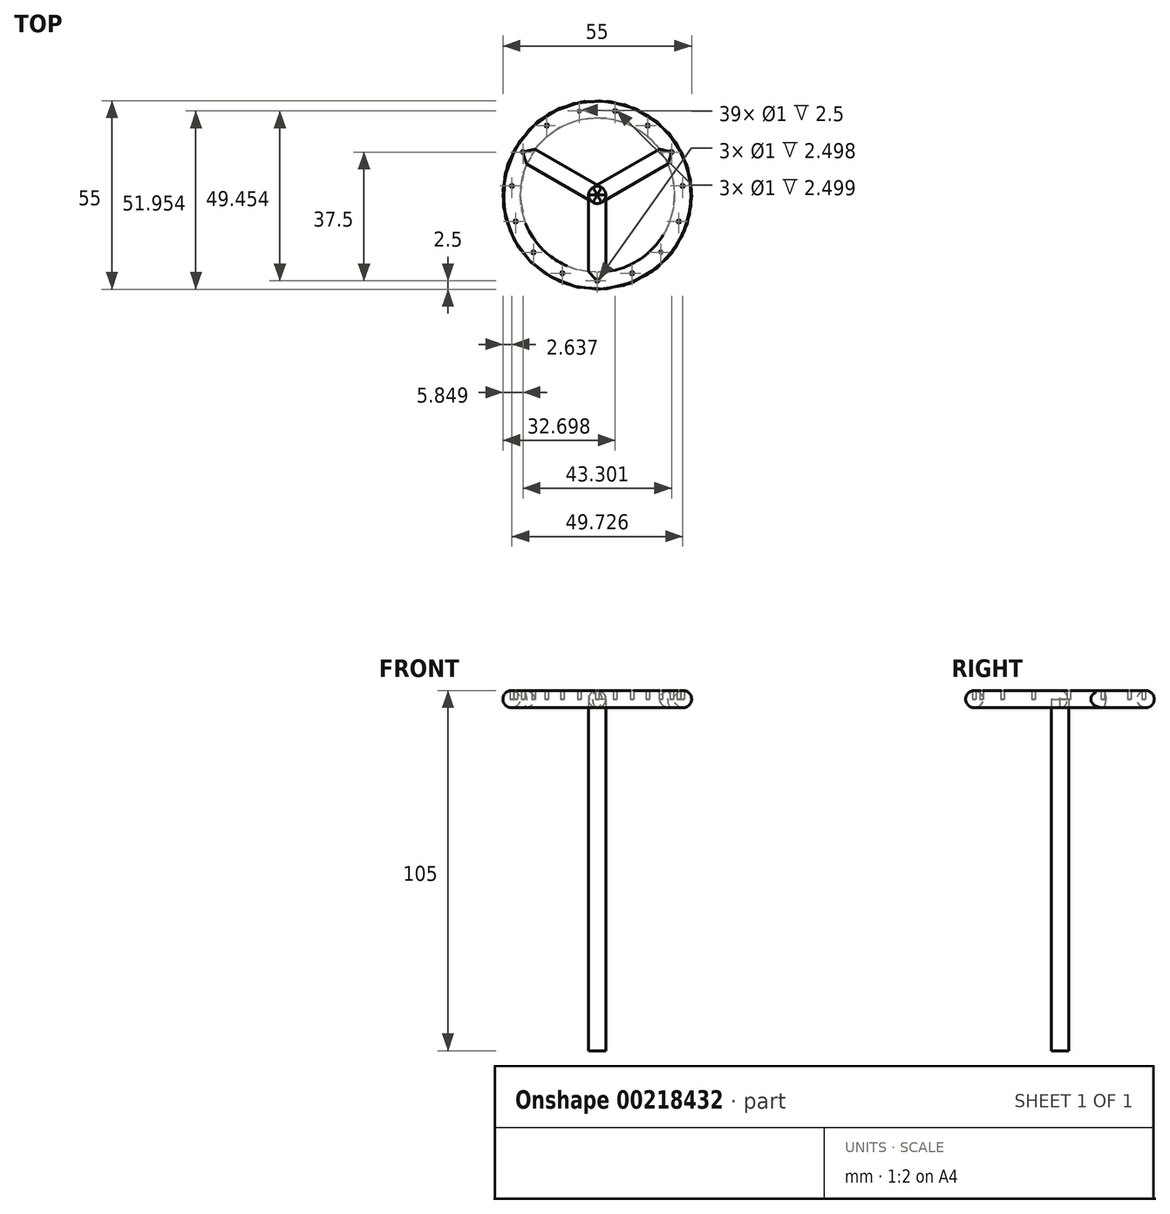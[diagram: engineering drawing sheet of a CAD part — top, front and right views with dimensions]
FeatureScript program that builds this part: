
annotation { "Feature Type Name" : "Feature", "Feature Type Description" : "" }
export const myFeature = defineFeature(function(context is Context, id is Id, definition is map)
    precondition{}
    {
        {
            var Q0;
            Q0=qCreatedBy(makeId("Top.planeOp"),FACE);
            var sketch = newSketch(context, id + "F0", { "sketchPlane" : qUnion([Q0])});
            skCircle(sketch, "E0", {"center": v(0, 0) * mm, "radius": 25 * mm});
            skLineSegment(sketch, "E1", {"start": v(0, 0) * mm, "end": v(-21.65, 12.5) * mm});
            skLineSegment(sketch, "E2", {"start": v(0, 0) * mm, "end": v(21.65, 12.5) * mm});
            skLineSegment(sketch, "E3", {"start": v(0, 0) * mm, "end": v(0, -25) * mm});
            skSolve(sketch);
        }
        {
            var Q0;
            Q0=qCreatedBy(makeId("Front.planeOp"),FACE);
            var sketch = newSketch(context, id + "F1", { "sketchPlane" : qUnion([Q0])});
            skLineSegment(sketch, "E4", {"start": v(0, 0) * mm, "end": v(0, -102.5) * mm});
            skSolve(sketch);
        }
        {
            var Q0;
            Q0=qCreatedBy(makeId("Front.planeOp"),FACE);
            var sketch = newSketch(context, id + "F2", { "sketchPlane" : qUnion([Q0])});
            skCircle(sketch, "E5", {"center": v(-25, 0) * mm, "radius": 2.5 * mm});
            skSolve(sketch);
        }
        {
            var Q0;
            Q0=makeQuery(id+"F2.imprint","IMPRINT",FACE,{"disambiguationData":[TD([[makeQuery(id+"F2.imprint","IMPRINT",EDGE,{"derivedFrom":sQuery(id+"F2.wireOp",EDGE,"E5")}),1.0]])]});
            var Q1;
            Q1=sQuery(id+"F0.wireOp",EDGE,"E0");
            sweep(context, id + "F3", {"profiles" : qUnion([Q0]), "path" : qUnion([Q1])});
        }
        {
            var Q0;
            Q0=qCreatedBy(makeId("Front.planeOp"),FACE);
            var sketch = newSketch(context, id + "F4", { "sketchPlane" : qUnion([Q0])});
            skCircle(sketch, "E6", {"center": v(0, 0) * mm, "radius": 2.5 * mm});
            skSolve(sketch);
        }
        {
            var Q0;
            Q0=makeQuery(id+"F4.imprint","IMPRINT",FACE,{"disambiguationData":[TD([[makeQuery(id+"F4.imprint","IMPRINT",EDGE,{"derivedFrom":sQuery(id+"F4.wireOp",EDGE,"E6")}),1.0]])]});
            var Q1;
            Q1=sQuery(id+"F0.wireOp",EDGE,"E3");
            sweep(context, id + "F5", {"operationType" : NewBodyOperationType.ADD, "profiles" : qUnion([Q0]), "path" : qUnion([Q1])});
        }
        {
            var Q0;
            Q0=makeQuery(id+"F3.opSweep","SWEPT_BODY",BODY,{"disambiguationData":[OSD([sQuery(id+"F0.wireOp",EDGE,"E0"),sQuery(id+"F2.wireOp",EDGE,"E5")])]});
            var Q1;
            Q1=sQuery(id+"F1.wireOp",EDGE,"E4");
            circularPattern(context, id + "F6", {"entities" : qUnion([Q0]), "axis" : qUnion([Q1]), "angle" : 360 * degree, "instanceCount" : 3, "equalSpace" : true});
        }
        {
            var Q0;
            Q0=qCreatedBy(makeId("Top.planeOp"),FACE);
            var sketch = newSketch(context, id + "F7", { "sketchPlane" : qUnion([Q0])});
            skCircle(sketch, "E7", {"center": v(0, 0) * mm, "radius": 2.5 * mm});
            skSolve(sketch);
        }
        {
            var Q0;
            Q0 = qSketchRegion(id + "F7", true);
            var Q1;
            Q1=sQuery(id+"F1.wireOp",EDGE,"E4");
            sweep(context, id + "F8", {"profiles" : qUnion([Q0]), "path" : qUnion([Q1])});
        }
        {
            var Q0;
            Q0=qCreatedBy(makeId("Top.planeOp"),FACE);
            var sketch = newSketch(context, id + "F9", { "sketchPlane" : qUnion([Q0])});
            skCircle(sketch, "E8", {"center": v(0, -25) * mm, "radius": 0.5 * mm});
            skSolve(sketch);
        }
        {
            var Q0;
            Q0 = qSketchRegion(id + "F9", true);
            extrude(context, id + "F10", {"entities" : qUnion([Q0]), "depth" : 2.5 * mm});
        }
        {
            var Q0;
            Q0=makeQuery(id+"F10.opExtrude","SWEPT_BODY",BODY,{"disambiguationData":[OSD([sQuery(id+"F9.wireOp",EDGE,"E8")])]});
            var Q1;
            Q1=sQuery(id+"F1.wireOp",EDGE,"E4");
            circularPattern(context, id + "F11", {"entities" : qUnion([Q0]), "axis" : qUnion([Q1]), "angle" : 360 * degree, "instanceCount" : 15, "equalSpace" : true});
        }
        {
            var Q0;
            Q0=makeQuery(id+"F11.opPattern","COPY",BODY,{"derivedFrom":makeQuery(id+"F10.opExtrude","SWEPT_BODY",BODY,{"disambiguationData":[OSD([sQuery(id+"F9.wireOp",EDGE,"E8")])]}),"instanceName":"1"});
            var Q1;
            Q1=makeQuery(id+"F11.opPattern","COPY",BODY,{"derivedFrom":makeQuery(id+"F10.opExtrude","SWEPT_BODY",BODY,{"disambiguationData":[OSD([sQuery(id+"F9.wireOp",EDGE,"E8")])]}),"instanceName":"23"});
            var Q2;
            Q2=makeQuery(id+"F11.opPattern","COPY",BODY,{"derivedFrom":makeQuery(id+"F10.opExtrude","SWEPT_BODY",BODY,{"disambiguationData":[OSD([sQuery(id+"F9.wireOp",EDGE,"E8")])]}),"instanceName":"22"});
            var Q3;
            Q3=makeQuery(id+"F11.opPattern","COPY",BODY,{"derivedFrom":makeQuery(id+"F10.opExtrude","SWEPT_BODY",BODY,{"disambiguationData":[OSD([sQuery(id+"F9.wireOp",EDGE,"E8")])]}),"instanceName":"21"});
            var Q4;
            Q4=makeQuery(id+"F11.opPattern","COPY",BODY,{"derivedFrom":makeQuery(id+"F10.opExtrude","SWEPT_BODY",BODY,{"disambiguationData":[OSD([sQuery(id+"F9.wireOp",EDGE,"E8")])]}),"instanceName":"20"});
            var Q5;
            Q5=makeQuery(id+"F11.opPattern","COPY",BODY,{"derivedFrom":makeQuery(id+"F10.opExtrude","SWEPT_BODY",BODY,{"disambiguationData":[OSD([sQuery(id+"F9.wireOp",EDGE,"E8")])]}),"instanceName":"19"});
            var Q6;
            Q6=makeQuery(id+"F11.opPattern","COPY",BODY,{"derivedFrom":makeQuery(id+"F10.opExtrude","SWEPT_BODY",BODY,{"disambiguationData":[OSD([sQuery(id+"F9.wireOp",EDGE,"E8")])]}),"instanceName":"18"});
            var Q7;
            Q7=makeQuery(id+"F11.opPattern","COPY",BODY,{"derivedFrom":makeQuery(id+"F10.opExtrude","SWEPT_BODY",BODY,{"disambiguationData":[OSD([sQuery(id+"F9.wireOp",EDGE,"E8")])]}),"instanceName":"17"});
            var Q8;
            Q8=makeQuery(id+"F11.opPattern","COPY",BODY,{"derivedFrom":makeQuery(id+"F10.opExtrude","SWEPT_BODY",BODY,{"disambiguationData":[OSD([sQuery(id+"F9.wireOp",EDGE,"E8")])]}),"instanceName":"16"});
            var Q9;
            Q9=makeQuery(id+"F11.opPattern","COPY",BODY,{"derivedFrom":makeQuery(id+"F10.opExtrude","SWEPT_BODY",BODY,{"disambiguationData":[OSD([sQuery(id+"F9.wireOp",EDGE,"E8")])]}),"instanceName":"15"});
            var Q10;
            Q10=makeQuery(id+"F11.opPattern","COPY",BODY,{"derivedFrom":makeQuery(id+"F10.opExtrude","SWEPT_BODY",BODY,{"disambiguationData":[OSD([sQuery(id+"F9.wireOp",EDGE,"E8")])]}),"instanceName":"14"});
            var Q11;
            Q11=makeQuery(id+"F11.opPattern","COPY",BODY,{"derivedFrom":makeQuery(id+"F10.opExtrude","SWEPT_BODY",BODY,{"disambiguationData":[OSD([sQuery(id+"F9.wireOp",EDGE,"E8")])]}),"instanceName":"13"});
            var Q12;
            Q12=makeQuery(id+"F11.opPattern","COPY",BODY,{"derivedFrom":makeQuery(id+"F10.opExtrude","SWEPT_BODY",BODY,{"disambiguationData":[OSD([sQuery(id+"F9.wireOp",EDGE,"E8")])]}),"instanceName":"12"});
            var Q13;
            Q13=makeQuery(id+"F11.opPattern","COPY",BODY,{"derivedFrom":makeQuery(id+"F10.opExtrude","SWEPT_BODY",BODY,{"disambiguationData":[OSD([sQuery(id+"F9.wireOp",EDGE,"E8")])]}),"instanceName":"11"});
            var Q14;
            Q14=makeQuery(id+"F11.opPattern","COPY",BODY,{"derivedFrom":makeQuery(id+"F10.opExtrude","SWEPT_BODY",BODY,{"disambiguationData":[OSD([sQuery(id+"F9.wireOp",EDGE,"E8")])]}),"instanceName":"10"});
            var Q15;
            Q15=makeQuery(id+"F11.opPattern","COPY",BODY,{"derivedFrom":makeQuery(id+"F10.opExtrude","SWEPT_BODY",BODY,{"disambiguationData":[OSD([sQuery(id+"F9.wireOp",EDGE,"E8")])]}),"instanceName":"9"});
            var Q16;
            Q16=makeQuery(id+"F11.opPattern","COPY",BODY,{"derivedFrom":makeQuery(id+"F10.opExtrude","SWEPT_BODY",BODY,{"disambiguationData":[OSD([sQuery(id+"F9.wireOp",EDGE,"E8")])]}),"instanceName":"8"});
            var Q17;
            Q17=makeQuery(id+"F11.opPattern","COPY",BODY,{"derivedFrom":makeQuery(id+"F10.opExtrude","SWEPT_BODY",BODY,{"disambiguationData":[OSD([sQuery(id+"F9.wireOp",EDGE,"E8")])]}),"instanceName":"7"});
            var Q18;
            Q18=makeQuery(id+"F11.opPattern","COPY",BODY,{"derivedFrom":makeQuery(id+"F10.opExtrude","SWEPT_BODY",BODY,{"disambiguationData":[OSD([sQuery(id+"F9.wireOp",EDGE,"E8")])]}),"instanceName":"6"});
            var Q19;
            Q19=makeQuery(id+"F11.opPattern","COPY",BODY,{"derivedFrom":makeQuery(id+"F10.opExtrude","SWEPT_BODY",BODY,{"disambiguationData":[OSD([sQuery(id+"F9.wireOp",EDGE,"E8")])]}),"instanceName":"5"});
            var Q20;
            Q20=makeQuery(id+"F11.opPattern","COPY",BODY,{"derivedFrom":makeQuery(id+"F10.opExtrude","SWEPT_BODY",BODY,{"disambiguationData":[OSD([sQuery(id+"F9.wireOp",EDGE,"E8")])]}),"instanceName":"4"});
            var Q21;
            Q21=makeQuery(id+"F11.opPattern","COPY",BODY,{"derivedFrom":makeQuery(id+"F10.opExtrude","SWEPT_BODY",BODY,{"disambiguationData":[OSD([sQuery(id+"F9.wireOp",EDGE,"E8")])]}),"instanceName":"3"});
            var Q22;
            Q22=makeQuery(id+"F11.opPattern","COPY",BODY,{"derivedFrom":makeQuery(id+"F10.opExtrude","SWEPT_BODY",BODY,{"disambiguationData":[OSD([sQuery(id+"F9.wireOp",EDGE,"E8")])]}),"instanceName":"2"});
            var Q23;
            Q23=makeQuery(id+"FsdLYlgyIIPtPH4_3.opPattern","COPY",BODY,{"derivedFrom":makeQuery(id+"F10.opExtrude","SWEPT_BODY",BODY,{"disambiguationData":[OSD([sQuery(id+"F9.wireOp",EDGE,"E8")])]}),"instanceName":"1"});
            var Q24;
            Q24=makeQuery(id+"FsdLYlgyIIPtPH4_3.opPattern","COPY",BODY,{"derivedFrom":makeQuery(id+"F10.opExtrude","SWEPT_BODY",BODY,{"disambiguationData":[OSD([sQuery(id+"F9.wireOp",EDGE,"E8")])]}),"instanceName":"2"});
            var Q25;
            Q25=makeQuery(id+"F10.opExtrude","SWEPT_BODY",BODY,{"disambiguationData":[OSD([sQuery(id+"F9.wireOp",EDGE,"E8")])]});
            var Q26;
            Q26=makeQuery(id+"FsdLYlgyIIPtPH4_3.opPattern","COPY",BODY,{"derivedFrom":makeQuery(id+"F10.opExtrude","SWEPT_BODY",BODY,{"disambiguationData":[OSD([sQuery(id+"F9.wireOp",EDGE,"E8")])]}),"instanceName":"3"});
            var Q27;
            Q27=makeQuery(id+"FsdLYlgyIIPtPH4_3.opPattern","COPY",BODY,{"derivedFrom":makeQuery(id+"F10.opExtrude","SWEPT_BODY",BODY,{"disambiguationData":[OSD([sQuery(id+"F9.wireOp",EDGE,"E8")])]}),"instanceName":"4"});
            var Q28;
            Q28=makeQuery(id+"F6GWW6hKw0zD2fU_3.opPattern","COPY",BODY,{"derivedFrom":makeQuery(id+"FsdLYlgyIIPtPH4_3.opPattern","COPY",BODY,{"derivedFrom":makeQuery(id+"F10.opExtrude","SWEPT_BODY",BODY,{"disambiguationData":[OSD([sQuery(id+"F9.wireOp",EDGE,"E8")])]}),"instanceName":"4"}),"instanceName":"1"});
            var Q29;
            Q29=makeQuery(id+"F6GWW6hKw0zD2fU_3.opPattern","COPY",BODY,{"derivedFrom":makeQuery(id+"FsdLYlgyIIPtPH4_3.opPattern","COPY",BODY,{"derivedFrom":makeQuery(id+"F10.opExtrude","SWEPT_BODY",BODY,{"disambiguationData":[OSD([sQuery(id+"F9.wireOp",EDGE,"E8")])]}),"instanceName":"3"}),"instanceName":"1"});
            var Q30;
            Q30=makeQuery(id+"F6GWW6hKw0zD2fU_3.opPattern","COPY",BODY,{"derivedFrom":makeQuery(id+"FsdLYlgyIIPtPH4_3.opPattern","COPY",BODY,{"derivedFrom":makeQuery(id+"F10.opExtrude","SWEPT_BODY",BODY,{"disambiguationData":[OSD([sQuery(id+"F9.wireOp",EDGE,"E8")])]}),"instanceName":"2"}),"instanceName":"1"});
            var Q31;
            Q31=makeQuery(id+"F6GWW6hKw0zD2fU_3.opPattern","COPY",BODY,{"derivedFrom":makeQuery(id+"FsdLYlgyIIPtPH4_3.opPattern","COPY",BODY,{"derivedFrom":makeQuery(id+"F10.opExtrude","SWEPT_BODY",BODY,{"disambiguationData":[OSD([sQuery(id+"F9.wireOp",EDGE,"E8")])]}),"instanceName":"1"}),"instanceName":"1"});
            var Q32;
            Q32=makeQuery(id+"F6GWW6hKw0zD2fU_3.opPattern","COPY",BODY,{"derivedFrom":makeQuery(id+"FsdLYlgyIIPtPH4_3.opPattern","COPY",BODY,{"derivedFrom":makeQuery(id+"F10.opExtrude","SWEPT_BODY",BODY,{"disambiguationData":[OSD([sQuery(id+"F9.wireOp",EDGE,"E8")])]}),"instanceName":"4"}),"instanceName":"2"});
            var Q33;
            Q33=makeQuery(id+"FsdLYlgyIIPtPH4_3.opPattern","COPY",BODY,{"derivedFrom":makeQuery(id+"F10.opExtrude","SWEPT_BODY",BODY,{"disambiguationData":[OSD([sQuery(id+"F9.wireOp",EDGE,"E8")])]}),"instanceName":"5"});
            var Q34;
            Q34=makeQuery(id+"F6GWW6hKw0zD2fU_3.opPattern","COPY",BODY,{"derivedFrom":makeQuery(id+"FsdLYlgyIIPtPH4_3.opPattern","COPY",BODY,{"derivedFrom":makeQuery(id+"F10.opExtrude","SWEPT_BODY",BODY,{"disambiguationData":[OSD([sQuery(id+"F9.wireOp",EDGE,"E8")])]}),"instanceName":"3"}),"instanceName":"2"});
            var Q35;
            Q35=makeQuery(id+"F6GWW6hKw0zD2fU_3.opPattern","COPY",BODY,{"derivedFrom":makeQuery(id+"FsdLYlgyIIPtPH4_3.opPattern","COPY",BODY,{"derivedFrom":makeQuery(id+"F10.opExtrude","SWEPT_BODY",BODY,{"disambiguationData":[OSD([sQuery(id+"F9.wireOp",EDGE,"E8")])]}),"instanceName":"2"}),"instanceName":"2"});
            var Q36;
            Q36=makeQuery(id+"F6GWW6hKw0zD2fU_3.opPattern","COPY",BODY,{"derivedFrom":makeQuery(id+"FsdLYlgyIIPtPH4_3.opPattern","COPY",BODY,{"derivedFrom":makeQuery(id+"F10.opExtrude","SWEPT_BODY",BODY,{"disambiguationData":[OSD([sQuery(id+"F9.wireOp",EDGE,"E8")])]}),"instanceName":"1"}),"instanceName":"2"});
            var Q37;
            Q37=makeQuery(id+"F6GWW6hKw0zD2fU_3.opPattern","COPY",BODY,{"derivedFrom":makeQuery(id+"FsdLYlgyIIPtPH4_3.opPattern","COPY",BODY,{"derivedFrom":makeQuery(id+"F10.opExtrude","SWEPT_BODY",BODY,{"disambiguationData":[OSD([sQuery(id+"F9.wireOp",EDGE,"E8")])]}),"instanceName":"5"}),"instanceName":"1"});
            var Q38;
            Q38=makeQuery(id+"F3.opSweep","SWEPT_BODY",BODY,{"disambiguationData":[OSD([sQuery(id+"F0.wireOp",EDGE,"E0"),sQuery(id+"F2.wireOp",EDGE,"E5")])]});
            var Q39;
            Q39=makeQuery(id+"F6.opPattern","COPY",BODY,{"derivedFrom":makeQuery(id+"F3.opSweep","SWEPT_BODY",BODY,{"disambiguationData":[OSD([sQuery(id+"F0.wireOp",EDGE,"E0"),sQuery(id+"F2.wireOp",EDGE,"E5")])]}),"instanceName":"1"});
            var Q40;
            Q40=makeQuery(id+"F8.opSweep","SWEPT_BODY",BODY,{"disambiguationData":[OSD([sQuery(id+"F1.wireOp",EDGE,"E4"),sQuery(id+"F7.wireOp",EDGE,"E7")])]});
            var Q41;
            Q41=makeQuery(id+"F6.opPattern","COPY",BODY,{"derivedFrom":makeQuery(id+"F3.opSweep","SWEPT_BODY",BODY,{"disambiguationData":[OSD([sQuery(id+"F0.wireOp",EDGE,"E0"),sQuery(id+"F2.wireOp",EDGE,"E5")])]}),"instanceName":"2"});
            booleanBodies(context, id + "F12", {"operationType" : BooleanOperationType.SUBTRACTION, "tools" : qUnion([Q0, Q1, Q2, Q3, Q4, Q5, Q6, Q7, Q8, Q9, Q10, Q11, Q12, Q13, Q14, Q15, Q16, Q17, Q18, Q19, Q20, Q21, Q22, Q23, Q24, Q25, Q26, Q27, Q28, Q29, Q30, Q31, Q32, Q33, Q34, Q35, Q36, Q37]), "targets" : qUnion([Q38, Q39, Q40, Q41])});
        }
    });
